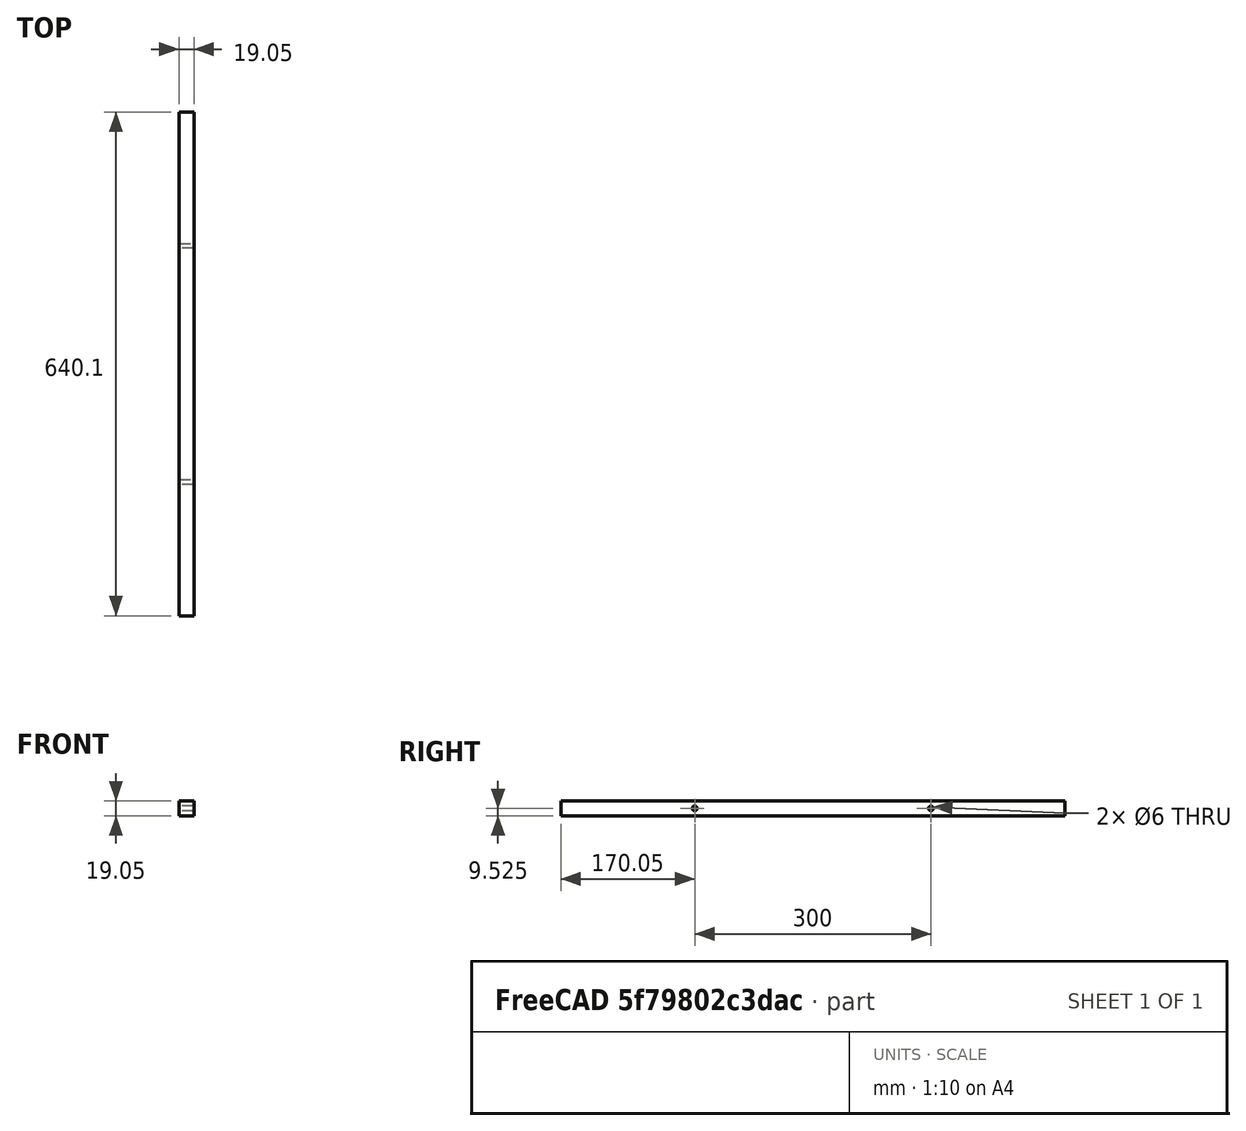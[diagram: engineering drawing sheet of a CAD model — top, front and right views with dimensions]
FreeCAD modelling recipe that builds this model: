
FCSTD DOCUMENT  (FreeCAD 0.20R29177 (Git))
Label: seamConnect
License: All rights reserved
LicenseURL: http://en.wikipedia.org/wiki/All_rights_reserved
objects: Sketcher::SketchObject×1, PartDesign::Pad×1, PartDesign::Body×1
note: 4 computed .brp shape members not serialized (recipe doc carries the construction recipe); baked Part::Feature solids carry a one-line shape summary decoded from their .brp

FEATURE [Sketcher::SketchObject] Sketch
  FullyConstrained = true
  MapMode = 5
  Placement = pos=(0,0,0) rot=(0.57735,0.57735,0.57735;2.0944rad)
  Support = -> [YZ_Plane]
  expr: Constraints[10] = 3 / 4 * 25.4
  expr: Constraints[9] = 650.1 - 5 - 5
  sketch-geometry (8):
    g0: LineSegment StartX=0 StartY=0 StartZ=0 EndX=640.1 EndY=0 EndZ=0
    g1: LineSegment StartX=640.1 StartY=0 StartZ=0 EndX=640.1 EndY=19.05 EndZ=0
    g2: LineSegment StartX=640.1 StartY=19.05 StartZ=0 EndX=0 EndY=19.05 EndZ=0
    g3: LineSegment StartX=0 StartY=19.05 StartZ=0 EndX=0 EndY=0 EndZ=0
    g4: LineSegment StartX=320.05 StartY=0 StartZ=0 EndX=320.05 EndY=19.05 EndZ=0
    g5: Circle CenterX=170.05 CenterY=9.525 CenterZ=0 NormalX=0 NormalY=0 NormalZ=1 AngleXU=0 Radius=3
    g6: Circle CenterX=470.05 CenterY=9.525 CenterZ=0 NormalX=0 NormalY=0 NormalZ=1 AngleXU=0 Radius=3
    g7: LineSegment StartX=2.2e-15 StartY=9.525 StartZ=0 EndX=640.1 EndY=9.525 EndZ=0
  constraints (23):
    c: Coincident(g0,g1)
    c: Coincident(g1,g2)
    c: Coincident(g2,g3)
    c: Coincident(g3,g0)
    c: Horizontal(g0)
    c: Horizontal(g2)
    c: Vertical(g1)
    c: Vertical(g3)
    c: Coincident(g0,g-1)
    c: DistanceX(g0,g0) = 640.1
    c: DistanceY(g3,g3) = 19.05
    c: Symmetric(g0,g0,g4)
    c: PointOnObject(g4,g2)
    c: Parallel(g4,g3)
    c: DistanceX(g5,g4) = 150
    c: Diameter(g5) = 6
    c: Diameter(g6) = 6
    c: DistanceX(g4,g6) = 150
    c: Horizontal(g7)
    c: Symmetric(g2,g0,g7)
    c: PointOnObject(g7,g1)
    c: PointOnObject(g5,g7)
    c: PointOnObject(g6,g7)
FEATURE [PartDesign::Pad] Pad
  Direction = (1,-2e-16,3e-16)
  Length = 19.05
  Length2 = 10
  Placement = pos=(0,0,0) rot=(0.57735,0.57735,0.57735;2.0944rad)
  Profile = -> Sketch
  ReferenceAxis = -> Sketch [N_Axis]
  Type = 0
  expr: Length = 3 / 4 * 25.4
FEATURE [PartDesign::Body] Body
  Group = -> [Sketch,Pad]
  Origin = -> Origin
  Tip = -> Pad
